# Revit family: ITK_Патч-панель_19-дюймовое крепление_1U_категория 6
name_source: partatom
category: Обобщенные модели
units: mm (PartAtom-declared; Revit-internal decimal feet)

## family parameters
Всегда вертикально = Да
Может служить основой для арматурных стержней = Нет
На основе рабочей плоскости = Нет
Общий = Нет
При загрузке вырезать с полостями = Нет
Размер круглого соединителя = Использовать диаметр
Тип детали = Нормальный
Точка расчета площади = Нет

## types (1)
- PP24-1UC6U-D05
    ADSK_URL страницы изделия = https://www.itk-group.ru
    ADSK_Версия Revit = 2019
    ADSK_Версия семейства = 1.0
    ADSK_Группирование = I. ЩИТЫ И ПУЛЬТЫ
    ADSK_Единица измерения = шт
    ADSK_Завод-изготовитель = IEK
    ADSK_Код изделия = PP24-1UC6U-D05
    ADSK_Масса = 1
    ADSK_Материал наименование = Металл и АБС-пластик
    ADSK_Наименование = ITK 1U патч-панель кат.6 UTP, 24 порта (Dual)
    IEK_URL = https://www.itk-group.ru
    IEK_Описание = Соответствие международным стандартам и ГОСТ Р.
Двойная понятная маркировка IDC-модулей и портов.
Расширенный частотный диапазон работы.
Увеличенное количество циклов включения-отключения.
Совместимы со всеми 19" шкафами и стойками ITK.
Подходят для кабелей и патч-кордов диаметром 22-26 AWG всех производителей.
Применимы для сетей ISDN, 10baseT, 100baseT, 1000baseT, EIA RS 232/485, 155 Mbit ATM, Token Ring.
    IEK_Цена за единицу = 3299.04
    KSI_CMa_Строительные материалы = 10.03.02.06
    KSI_CPr_Строительные изделия = 27.12.31.61.1.04.09-1090
    URL = https://www.iek.ru
    Высота = 44 мм
    Глубина = 37 мм
    Изготовитель = ITK
    Материал = Окраска - RAL 9005
    Ширина = 483 мм
